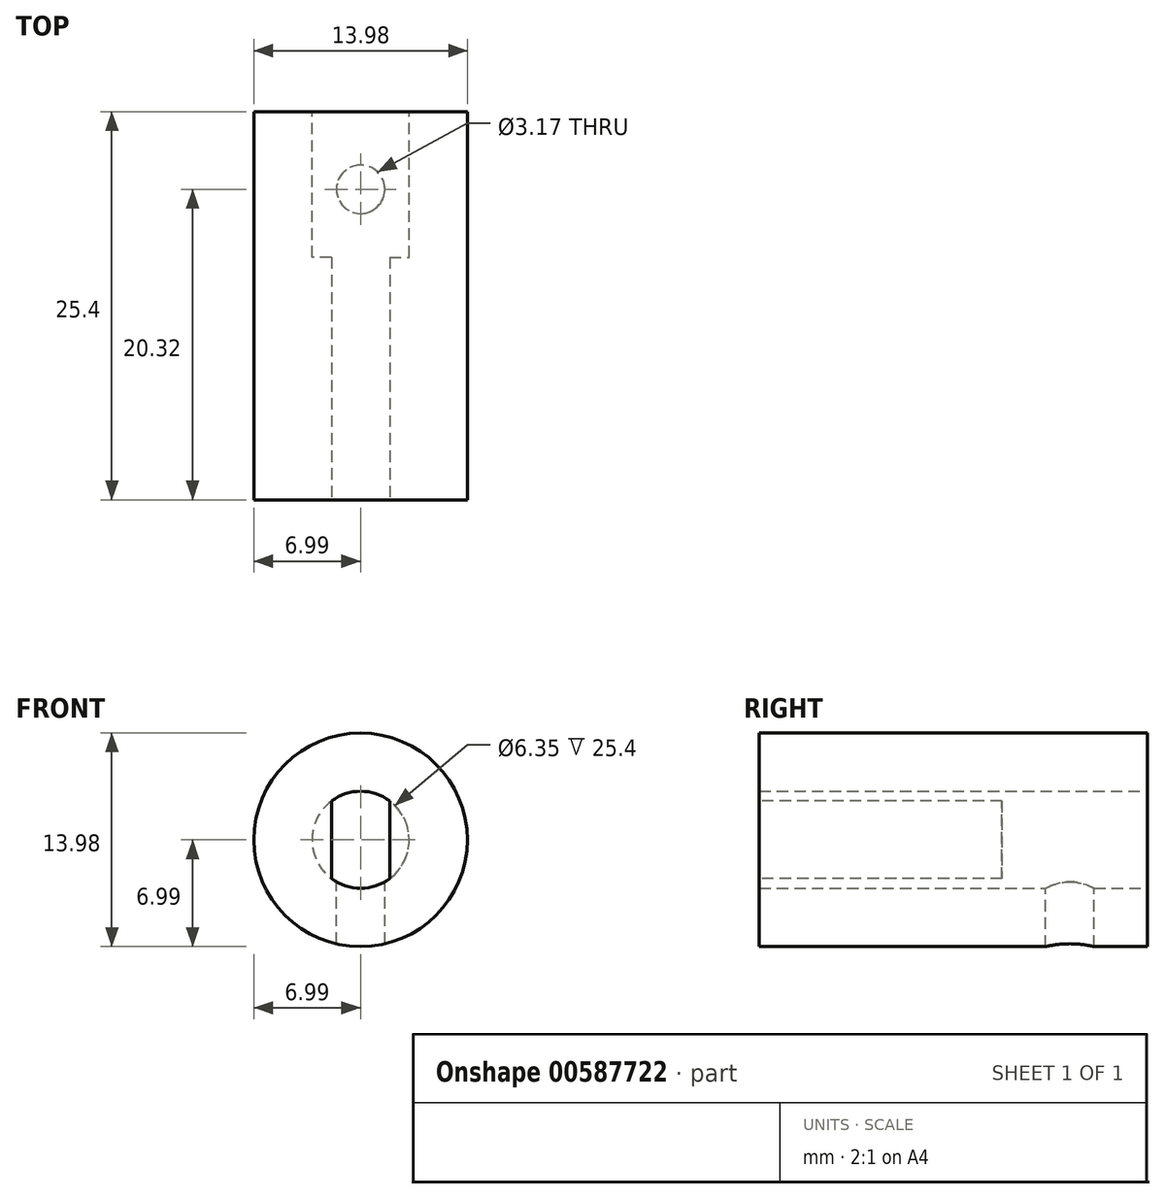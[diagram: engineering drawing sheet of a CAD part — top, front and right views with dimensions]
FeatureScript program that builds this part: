
annotation { "Feature Type Name" : "Feature", "Feature Type Description" : "" }
export const myFeature = defineFeature(function(context is Context, id is Id, definition is map)
    precondition{}
    {
        {
            var Q0;
            Q0=qCreatedBy(makeId("Front.planeOp"),FACE);
            var sketch = newSketch(context, id + "F0", { "sketchPlane" : qUnion([Q0])});
            skCircle(sketch, "E0", {"center": v(0, 0) * mm, "radius": 3.18 * mm});
            skCircle(sketch, "E1", {"center": v(0, 0) * mm, "radius": 6.99 * mm});
            skSolve(sketch);
        }
        {
            var Q0;
            Q0 = qSketchRegion(id + "F0", true);
            var Q1;
            Q1=makeQuery(id+"F0.imprint","IMPRINT",FACE,{"disambiguationData":[TD([[makeQuery(id+"F0.imprint","IMPRINT",EDGE,{"derivedFrom":sQuery(id+"F0.wireOp",EDGE,"E0")}),1.0]])]});
            extrude(context, id + "F1", {"entities" : qUnion([Q0, Q1]), "depth" : 25.4 * mm, "offsetDistance" : 25.4 * mm});
        }
        {
            var Q0;
            Q0=makeQuery(id+"F0.imprint","IMPRINT",FACE,{"disambiguationData":[TD([[makeQuery(id+"F0.imprint","IMPRINT",EDGE,{"derivedFrom":sQuery(id+"F0.wireOp",EDGE,"E0")}),1.0]])]});
            extrude(context, id + "F2", {"entities" : qUnion([Q0]), "operationType" : NewBodyOperationType.REMOVE, "depth" : 9.52 * mm, "offsetDistance" : 25.4 * mm});
        }
        {
            var Q0;
            Q0=makeQuery(id+"F1.opExtrude","CAP_FACE",FACE,{"disambiguationData":[OSD([sQuery(id+"F0.wireOp",EDGE,"E1")])],"isStart":false});
            var sketch = newSketch(context, id + "F3", { "sketchPlane" : qUnion([Q0])});
            skArc(sketch, "E2", {"start": v(-1.9, -2.54) * mm, "mid": v(0, -3.18) * mm, "end": v(1.9, -2.54) * mm});
            skLineSegment(sketch, "E3", {"start": v(-1.9, 2.54) * mm, "end": v(-1.9, -2.54) * mm});
            skLineSegment(sketch, "E4", {"start": v(1.9, 2.54) * mm, "end": v(1.9, -2.54) * mm});
            skArc(sketch, "E5.trimOffspring", {"start": v(1.9, 2.54) * mm, "mid": v(0, 3.18) * mm, "end": v(-1.9, 2.54) * mm});
            skSolve(sketch);
        }
        {
            var Q0;
            Q0 = qSketchRegion(id + "F3", true);
            extrude(context, id + "F4", {"entities" : qUnion([Q0]), "operationType" : NewBodyOperationType.REMOVE, "oppositeDirection" : true, "depth" : 25.4 * mm, "offsetDistance" : 25.4 * mm});
        }
        {
            var Q0;
            Q0=qCreatedBy(makeId("Top.planeOp"),FACE);
            var sketch = newSketch(context, id + "F5", { "sketchPlane" : qUnion([Q0])});
            skCircle(sketch, "E6", {"center": v(0, -5.08) * mm, "radius": 1.59 * mm});
            skSolve(sketch);
        }
        {
            var Q0;
            Q0 = qSketchRegion(id + "F5", true);
            extrude(context, id + "F6", {"entities" : qUnion([Q0]), "operationType" : NewBodyOperationType.REMOVE, "oppositeDirection" : true, "depth" : 25.4 * mm, "offsetDistance" : 25.4 * mm});
        }
    });
